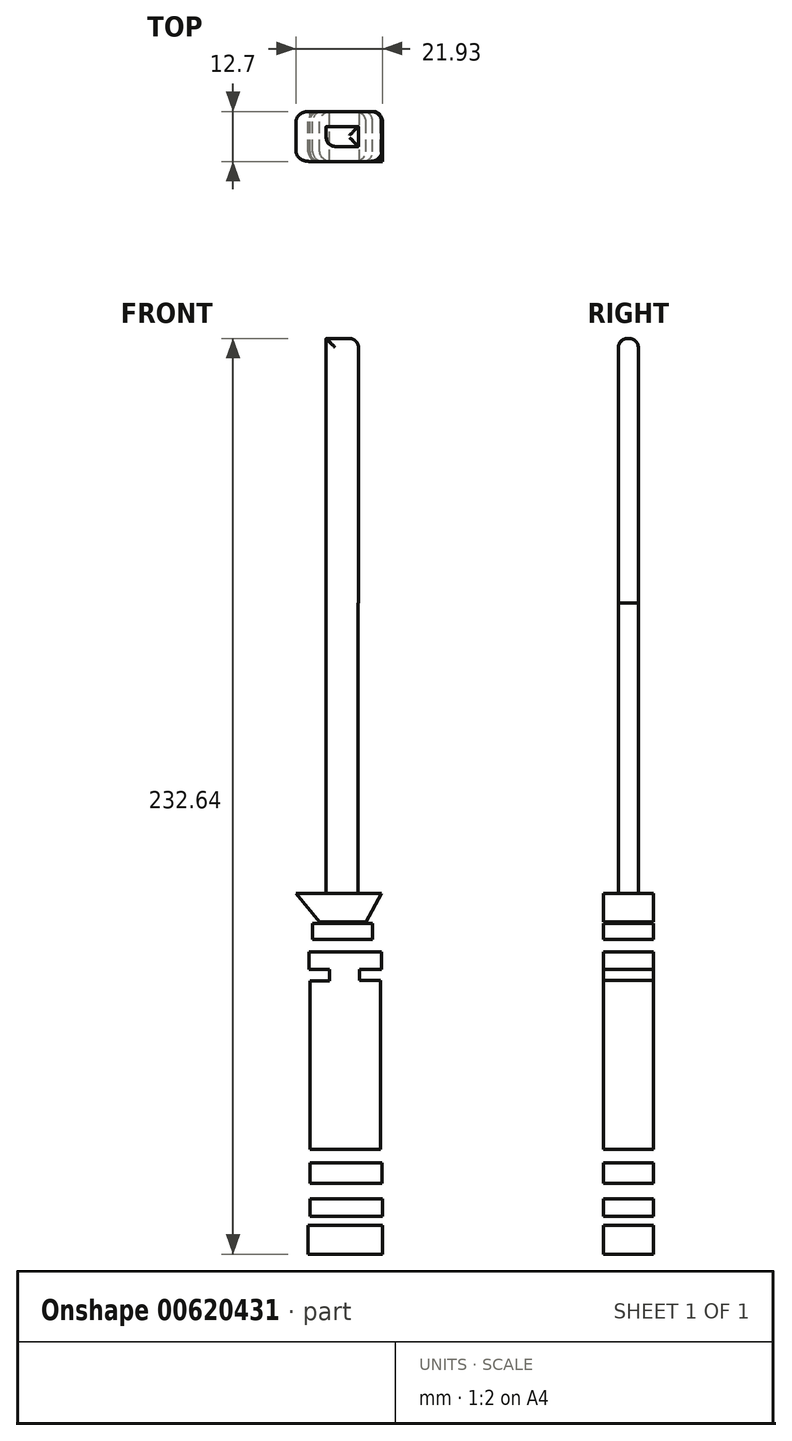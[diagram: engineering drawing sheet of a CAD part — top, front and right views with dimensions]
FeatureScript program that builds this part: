
annotation { "Feature Type Name" : "Feature", "Feature Type Description" : "" }
export const myFeature = defineFeature(function(context is Context, id is Id, definition is map)
    precondition{}
    {
        {
            var Q0;
            Q0=qCreatedBy(makeId("Front.planeOp"),FACE);
            var sketch = newSketch(context, id + "F0", { "sketchPlane" : qUnion([Q0])});
            skLineSegment(sketch, "E0", {"start": v(-11.68, 17.85) * mm, "end": v(-5.77, 10.6) * mm});
            skLineSegment(sketch, "E1", {"start": v(-5.77, 10.6) * mm, "end": v(6.04, 10.6) * mm});
            skLineSegment(sketch, "E2", {"start": v(6.04, 10.6) * mm, "end": v(10.07, 17.85) * mm});
            skLineSegment(sketch, "E3", {"start": v(10.07, 17.85) * mm, "end": v(-11.68, 17.85) * mm});
            skPoint(sketch, "E4.middle", {"position": v(0.13, -3.36) * mm});
            skPoint(sketch, "E5", {"position": v(0.13, 10.6) * mm});
            skLineSegment(sketch, "E6.bottom", {"start": v(-7.47, 10.27) * mm, "end": v(7.78, 10.27) * mm});
            skLineSegment(sketch, "E6.top", {"start": v(-7.47, 6.2) * mm, "end": v(7.78, 6.2) * mm});
            skLineSegment(sketch, "E6.left", {"start": v(-7.47, 10.27) * mm, "end": v(-7.47, 6.2) * mm});
            skLineSegment(sketch, "E6.right", {"start": v(7.78, 10.27) * mm, "end": v(7.78, 6.2) * mm});
            skLineSegment(sketch, "E7.bottom", {"start": v(-3.36, 6.2) * mm, "end": v(4.43, 6.2) * mm});
            skLineSegment(sketch, "E7.top", {"start": v(-3.36, 3.09) * mm, "end": v(4.43, 3.09) * mm});
            skLineSegment(sketch, "E7.left", {"start": v(-3.36, 6.2) * mm, "end": v(-3.36, 3.09) * mm});
            skLineSegment(sketch, "E7.right", {"start": v(4.43, 6.2) * mm, "end": v(4.43, 3.09) * mm});
            skLineSegment(sketch, "E8.bottom", {"start": v(-8.46, 3.09) * mm, "end": v(9.99, 3.09) * mm});
            skLineSegment(sketch, "E8.top", {"start": v(-8.46, -1.43) * mm, "end": v(9.99, -1.43) * mm});
            skLineSegment(sketch, "E8.left", {"start": v(-8.46, 3.09) * mm, "end": v(-8.46, -1.43) * mm});
            skLineSegment(sketch, "E8.right", {"start": v(9.99, 3.09) * mm, "end": v(9.99, -1.43) * mm});
            skLineSegment(sketch, "E9", {"start": v(-3.22, -1.43) * mm, "end": v(-3.22, -4.32) * mm});
            skLineSegment(sketch, "E10", {"start": v(-3.22, -4.32) * mm, "end": v(-8.17, -4.32) * mm});
            skLineSegment(sketch, "E11", {"start": v(-8.17, -4.32) * mm, "end": v(-8.17, -47.12) * mm});
            skLineSegment(sketch, "E12", {"start": v(-8.17, -47.12) * mm, "end": v(9.8, -47.12) * mm});
            skLineSegment(sketch, "E13", {"start": v(9.8, -47.12) * mm, "end": v(9.8, -4.16) * mm});
            skLineSegment(sketch, "E14", {"start": v(9.8, -4.16) * mm, "end": v(4.43, -4.16) * mm});
            skLineSegment(sketch, "E15", {"start": v(4.43, -4.16) * mm, "end": v(4.43, 0) * mm});
            skLineSegment(sketch, "E16.bottom", {"start": v(-3.6, -47.12) * mm, "end": v(5.72, -47.12) * mm});
            skLineSegment(sketch, "E16.top", {"start": v(-3.6, -50.57) * mm, "end": v(5.72, -50.57) * mm});
            skLineSegment(sketch, "E16.left", {"start": v(-3.6, -47.12) * mm, "end": v(-3.6, -50.57) * mm});
            skLineSegment(sketch, "E16.right", {"start": v(5.72, -47.12) * mm, "end": v(5.72, -50.57) * mm});
            skLineSegment(sketch, "E17.bottom", {"start": v(-8.17, -50.57) * mm, "end": v(10.16, -50.57) * mm});
            skLineSegment(sketch, "E17.top", {"start": v(-8.17, -55.74) * mm, "end": v(10.16, -55.74) * mm});
            skLineSegment(sketch, "E17.left", {"start": v(-8.17, -50.57) * mm, "end": v(-8.17, -55.74) * mm});
            skLineSegment(sketch, "E17.right", {"start": v(10.16, -50.57) * mm, "end": v(10.16, -55.74) * mm});
            skLineSegment(sketch, "E18.bottom", {"start": v(-3.37, -55.74) * mm, "end": v(5.72, -55.74) * mm});
            skLineSegment(sketch, "E18.top", {"start": v(-3.37, -59.71) * mm, "end": v(5.72, -59.71) * mm});
            skLineSegment(sketch, "E18.left", {"start": v(-3.37, -55.74) * mm, "end": v(-3.37, -59.71) * mm});
            skLineSegment(sketch, "E18.right", {"start": v(5.72, -55.74) * mm, "end": v(5.72, -59.71) * mm});
            skLineSegment(sketch, "E19.bottom", {"start": v(-8.2, -59.75) * mm, "end": v(10.25, -59.75) * mm});
            skLineSegment(sketch, "E19.top", {"start": v(-8.2, -64.2) * mm, "end": v(10.25, -64.2) * mm});
            skLineSegment(sketch, "E19.left", {"start": v(-8.2, -59.75) * mm, "end": v(-8.2, -64.2) * mm});
            skLineSegment(sketch, "E19.right", {"start": v(10.25, -59.75) * mm, "end": v(10.25, -64.2) * mm});
            skLineSegment(sketch, "E20.bottom", {"start": v(-5.75, -64.2) * mm, "end": v(7.8, -64.2) * mm});
            skLineSegment(sketch, "E20.top", {"start": v(-5.75, -66.42) * mm, "end": v(7.8, -66.42) * mm});
            skLineSegment(sketch, "E20.left", {"start": v(-5.75, -64.2) * mm, "end": v(-5.75, -66.42) * mm});
            skLineSegment(sketch, "E20.right", {"start": v(7.8, -64.2) * mm, "end": v(7.8, -66.42) * mm});
            skLineSegment(sketch, "E21.bottom", {"start": v(-8.64, -66.42) * mm, "end": v(10.25, -66.42) * mm});
            skLineSegment(sketch, "E21.top", {"start": v(-8.64, -73.75) * mm, "end": v(10.25, -73.75) * mm});
            skLineSegment(sketch, "E21.left", {"start": v(-8.64, -66.42) * mm, "end": v(-8.64, -73.75) * mm});
            skLineSegment(sketch, "E21.right", {"start": v(10.25, -66.42) * mm, "end": v(10.25, -73.75) * mm});
            skSolve(sketch);
        }
        {
            var Q0;
            Q0=makeQuery(id+"F0.imprint","IMPRINT",FACE,{"disambiguationData":[TD([[makeQuery(id+"F0.imprint","IMPRINT",EDGE,{"derivedFrom":sQuery(id+"F0.wireOp",EDGE,"E0")}),1.0]])]});
            var Q1;
            Q1=makeQuery(id+"F0.imprint","IMPRINT",FACE,{"disambiguationData":[TD([[makeQuery(id+"F0.imprint","IMPRINT",EDGE,{"derivedFrom":sQuery(id+"F0.wireOp",EDGE,"E6.bottom")}),-1.0]])]});
            var Q2;
            Q2=makeQuery(id+"F0.imprint","IMPRINT",FACE,{"disambiguationData":[TD([[makeQuery(id+"F0.imprint","IMPRINT",EDGE,{"derivedFrom":sQuery(id+"F0.wireOp",EDGE,"E7.bottom")}),-1.0]])]});
            var Q3;
            {var subQ0=sQuery(id+"F0.wireOp",EDGE,"E8.left");Q3=makeQuery(id+"F0.imprint","IMPRINT",FACE,{"disambiguationData":[TD([[makeQuery(id+"F0.imprint","IMPRINT",EDGE,{"derivedFrom":subQ0}),1.0]])]});}
            var Q4;
            {var subQ1=sQuery(id+"F0.wireOp",EDGE,"E9");Q4=makeQuery(id+"F0.imprint","IMPRINT",FACE,{"disambiguationData":[TD([[makeQuery(id+"F0.imprint","IMPRINT",EDGE,{"derivedFrom":subQ1}),1.0]])]});}
            var Q5;
            Q5=makeQuery(id+"F0.imprint","IMPRINT",FACE,{"disambiguationData":[TD([[makeQuery(id+"F0.imprint","IMPRINT",EDGE,{"derivedFrom":sQuery(id+"F0.wireOp",EDGE,"E16.bottom")}),-1.0]])]});
            var Q6;
            {var subQ0=sQuery(id+"F0.wireOp",EDGE,"E17.left");Q6=makeQuery(id+"F0.imprint","IMPRINT",FACE,{"disambiguationData":[TD([[makeQuery(id+"F0.imprint","IMPRINT",EDGE,{"derivedFrom":subQ0}),1.0]])]});}
            var Q7;
            Q7=makeQuery(id+"F0.imprint","IMPRINT",FACE,{"disambiguationData":[TD([[makeQuery(id+"F0.imprint","IMPRINT",EDGE,{"derivedFrom":sQuery(id+"F0.wireOp",EDGE,"E18.bottom")}),-1.0]])]});
            var Q8;
            Q8=makeQuery(id+"F0.imprint","IMPRINT",FACE,{"disambiguationData":[TD([[makeQuery(id+"F0.imprint","IMPRINT",EDGE,{"derivedFrom":sQuery(id+"F0.wireOp",EDGE,"E19.bottom")}),-1.0]])]});
            var Q9;
            Q9=makeQuery(id+"F0.imprint","IMPRINT",FACE,{"disambiguationData":[TD([[makeQuery(id+"F0.imprint","IMPRINT",EDGE,{"derivedFrom":sQuery(id+"F0.wireOp",EDGE,"E20.bottom")}),-1.0]])]});
            var Q10;
            Q10=makeQuery(id+"F0.imprint","IMPRINT",FACE,{"disambiguationData":[TD([[makeQuery(id+"F0.imprint","IMPRINT",EDGE,{"derivedFrom":sQuery(id+"F0.wireOp",EDGE,"E21.top")}),1.0]])]});
            extrude(context, id + "F1", {"entities" : qUnion([Q0, Q1, Q2, Q3, Q4, Q5, Q6, Q7, Q8, Q9, Q10]), "endBound" : BoundingType.SYMMETRIC, "depth" : 12.7 * mm, "offsetDistance" : 25.4 * mm});
        }
        {
            var Q0;
            Q0=qCreatedBy(makeId("Front.planeOp"),FACE);
            var sketch = newSketch(context, id + "F2", { "sketchPlane" : qUnion([Q0])});
            skLineSegment(sketch, "E22.bottom", {"start": v(0, 15.52) * mm, "end": v(4.04, 15.52) * mm});
            skLineSegment(sketch, "E22.top", {"start": v(0, 91.72) * mm, "end": v(4.04, 91.72) * mm});
            skLineSegment(sketch, "E22.left", {"start": v(0, 15.52) * mm, "end": v(0, 91.72) * mm});
            skLineSegment(sketch, "E22.right", {"start": v(4.04, 15.52) * mm, "end": v(4.04, 91.72) * mm});
            skLineSegment(sketch, "E23.MirrorCS", {"start": v(-4.04, 15.52) * mm, "end": v(-4.04, 91.72) * mm});
            skLineSegment(sketch, "E24.MirrorCS", {"start": v(0, 15.52) * mm, "end": v(-4.04, 15.52) * mm});
            skLineSegment(sketch, "E25.MirrorCS", {"start": v(0, 91.72) * mm, "end": v(-4.04, 91.72) * mm});
            skLineSegment(sketch, "E26.bottom", {"start": v(-4.04, 91.72) * mm, "end": v(4.16, 91.72) * mm});
            skLineSegment(sketch, "E26.top", {"start": v(-4.04, 158.9) * mm, "end": v(4.16, 158.9) * mm});
            skLineSegment(sketch, "E26.left", {"start": v(-4.04, 91.72) * mm, "end": v(-4.04, 158.9) * mm});
            skLineSegment(sketch, "E26.right", {"start": v(4.16, 91.72) * mm, "end": v(4.16, 158.9) * mm});
            skSolve(sketch);
        }
        {
            var Q0;
            Q0=makeQuery(id+"F1.opExtrude","CAP_EDGE",EDGE,{"disambiguationData":[OSD([sQuery(id+"F0.wireOp",EDGE,"E8.right")])],"isStart":false});
            var Q1;
            Q1=makeQuery(id+"F1.opExtrude","CAP_EDGE",EDGE,{"disambiguationData":[OSD([sQuery(id+"F0.wireOp",EDGE,"E8.left")])],"isStart":false});
            var Q2;
            Q2=makeQuery(id+"F1.opExtrude","CAP_EDGE",EDGE,{"disambiguationData":[OSD([sQuery(id+"F0.wireOp",EDGE,"E6.left")])],"isStart":false});
            var Q3;
            Q3=makeQuery(id+"F1.opExtrude","CAP_EDGE",EDGE,{"disambiguationData":[OSD([sQuery(id+"F0.wireOp",EDGE,"E6.right")])],"isStart":false});
            var Q4;
            Q4=makeQuery(id+"F1.opExtrude","CAP_EDGE",EDGE,{"disambiguationData":[OSD([sQuery(id+"F0.wireOp",EDGE,"E6.right")])],"isStart":true});
            var Q5;
            Q5=makeQuery(id+"F1.opExtrude","CAP_EDGE",EDGE,{"disambiguationData":[OSD([sQuery(id+"F0.wireOp",EDGE,"E8.right")])],"isStart":true});
            var Q6;
            Q6=makeQuery(id+"F1.opExtrude","CAP_EDGE",EDGE,{"disambiguationData":[OSD([sQuery(id+"F0.wireOp",EDGE,"E8.left")])],"isStart":true});
            var Q7;
            Q7=makeQuery(id+"F1.opExtrude","CAP_EDGE",EDGE,{"disambiguationData":[OSD([sQuery(id+"F0.wireOp",EDGE,"E6.left")])],"isStart":true});
            var Q8;
            Q8=makeQuery(id+"F1.opExtrude","CAP_EDGE",EDGE,{"disambiguationData":[OSD([sQuery(id+"F0.wireOp",EDGE,"E17.right")])],"isStart":false});
            var Q9;
            Q9=makeQuery(id+"F1.opExtrude","CAP_EDGE",EDGE,{"disambiguationData":[OSD([sQuery(id+"F0.wireOp",EDGE,"E17.right")])],"isStart":true});
            var Q10;
            Q10=makeQuery(id+"F1.opExtrude","CAP_EDGE",EDGE,{"disambiguationData":[OSD([sQuery(id+"F0.wireOp",EDGE,"E19.right")])],"isStart":false});
            var Q11;
            Q11=makeQuery(id+"F1.opExtrude","CAP_EDGE",EDGE,{"disambiguationData":[OSD([sQuery(id+"F0.wireOp",EDGE,"E17.left")])],"isStart":false});
            var Q12;
            Q12=makeQuery(id+"F1.opExtrude","CAP_EDGE",EDGE,{"disambiguationData":[OSD([sQuery(id+"F0.wireOp",EDGE,"E19.left")])],"isStart":false});
            var Q13;
            Q13=makeQuery(id+"F1.opExtrude","CAP_EDGE",EDGE,{"disambiguationData":[OSD([sQuery(id+"F0.wireOp",EDGE,"E21.left")])],"isStart":false});
            var Q14;
            Q14=makeQuery(id+"F1.opExtrude","CAP_EDGE",EDGE,{"disambiguationData":[OSD([sQuery(id+"F0.wireOp",EDGE,"E19.right")])],"isStart":true});
            var Q15;
            Q15=makeQuery(id+"F1.opExtrude","CAP_EDGE",EDGE,{"disambiguationData":[OSD([sQuery(id+"F0.wireOp",EDGE,"E21.right")])],"isStart":true});
            var Q16;
            Q16=makeQuery(id+"F1.opExtrude","CAP_EDGE",EDGE,{"disambiguationData":[OSD([sQuery(id+"F0.wireOp",EDGE,"E21.left")])],"isStart":true});
            var Q17;
            Q17=makeQuery(id+"F1.opExtrude","CAP_EDGE",EDGE,{"disambiguationData":[OSD([sQuery(id+"F0.wireOp",EDGE,"E19.left")])],"isStart":true});
            var Q18;
            Q18=makeQuery(id+"F1.opExtrude","CAP_EDGE",EDGE,{"disambiguationData":[OSD([sQuery(id+"F0.wireOp",EDGE,"E17.left")])],"isStart":true});
            var Q19;
            Q19=makeQuery(id+"F1.opExtrude","CAP_EDGE",EDGE,{"disambiguationData":[OSD([sQuery(id+"F0.wireOp",EDGE,"E11")])],"isStart":false});
            var Q20;
            Q20=makeQuery(id+"F1.opExtrude","CAP_EDGE",EDGE,{"disambiguationData":[OSD([sQuery(id+"F0.wireOp",EDGE,"E13")])],"isStart":false});
            var Q21;
            Q21=makeQuery(id+"F1.opExtrude","CAP_EDGE",EDGE,{"disambiguationData":[OSD([sQuery(id+"F0.wireOp",EDGE,"E13")])],"isStart":true});
            var Q22;
            Q22=makeQuery(id+"F1.opExtrude","CAP_EDGE",EDGE,{"disambiguationData":[OSD([sQuery(id+"F0.wireOp",EDGE,"E0")])],"isStart":false});
            var Q23;
            Q23=makeQuery(id+"F1.opExtrude","CAP_EDGE",EDGE,{"disambiguationData":[OSD([sQuery(id+"F0.wireOp",EDGE,"E2")])],"isStart":false});
            var Q24;
            Q24=makeQuery(id+"F1.opExtrude","CAP_EDGE",EDGE,{"disambiguationData":[OSD([sQuery(id+"F0.wireOp",EDGE,"E2")])],"isStart":true});
            var Q25;
            Q25=makeQuery(id+"F1.opExtrude","CAP_EDGE",EDGE,{"disambiguationData":[OSD([sQuery(id+"F0.wireOp",EDGE,"E0")])],"isStart":true});
            fillet(context, id + "F3", {"entities" : qUnion([Q0, Q1, Q2, Q3, Q4, Q5, Q6, Q7, Q8, Q9, Q10, Q11, Q12, Q13, Q14, Q15, Q16, Q17, Q18, Q19, Q20, Q21, Q22, Q23, Q24, Q25]), "radius" : 2.54 * mm, "tangentPropagation" : true, "allowEdgeOverflow" : false});
        }
        {
            var Q0;
            Q0=makeQuery(id+"F2.imprint","IMPRINT",FACE,{"disambiguationData":[TD([[makeQuery(id+"F2.imprint","IMPRINT",EDGE,{"derivedFrom":sQuery(id+"F2.wireOp",EDGE,"E22.bottom")}),1.0]])]});
            var Q1;
            Q1=makeQuery(id+"F2.imprint","IMPRINT",FACE,{"disambiguationData":[TD([[makeQuery(id+"F2.imprint","IMPRINT",EDGE,{"derivedFrom":sQuery(id+"F2.wireOp",EDGE,"E22.left")}),1.0]])]});
            var Q2;
            Q2=makeQuery(id+"F2.imprint","IMPRINT",FACE,{"disambiguationData":[TD([[makeQuery(id+"F2.imprint","IMPRINT",EDGE,{"derivedFrom":sQuery(id+"F2.wireOp",EDGE,"E26.top")}),-1.0]])]});
            extrude(context, id + "F4", {"entities" : qUnion([Q0, Q1, Q2]), "operationType" : NewBodyOperationType.ADD, "endBound" : BoundingType.SYMMETRIC, "depth" : 5.08 * mm, "offsetDistance" : 25.4 * mm});
        }
        {
            var Q0;
            Q0=makeQuery(id+"F4.opExtrude","SWEPT_EDGE",EDGE,{"disambiguationData":[OSD([sQuery(id+"F2.wireOp",EDGE,"E26.top"),sQuery(id+"F2.wireOp",EDGE,"E26.left")])]});
            var Q1;
            Q1=makeQuery(id+"F4.opExtrude","CAP_EDGE",EDGE,{"disambiguationData":[OSD([sQuery(id+"F2.wireOp",EDGE,"E22.right")])],"isStart":false});
            var Q2;
            Q2=makeQuery(id+"F4.opExtrude","CAP_EDGE",EDGE,{"disambiguationData":[OSD([sQuery(id+"F2.wireOp",EDGE,"E26.right")])],"isStart":false});
            var Q3;
            Q3=makeQuery(id+"F4.opExtrude","CAP_EDGE",EDGE,{"disambiguationData":[OSD([sQuery(id+"F2.wireOp",EDGE,"E26.right")])],"isStart":true});
            var Q4;
            Q4=makeQuery(id+"F4.opExtrude","CAP_EDGE",EDGE,{"disambiguationData":[OSD([sQuery(id+"F2.wireOp",EDGE,"E22.right")])],"isStart":true});
            var Q5;
            Q5=makeQuery(id+"F4.opExtrude","CAP_EDGE",EDGE,{"disambiguationData":[OSD([sQuery(id+"F2.wireOp",EDGE,"E23.MirrorCS"),sQuery(id+"F2.wireOp",EDGE,"E26.left")])],"isStart":true});
            fillet(context, id + "F5", {"entities" : qUnion([Q0, Q1, Q2, Q3, Q4, Q5]), "radius" : 0.03 * mm, "tangentPropagation" : true, "allowEdgeOverflow" : false});
        }
        {
            var Q0;
            Q0=makeQuery(id+"F4.opExtrude","CAP_EDGE",EDGE,{"disambiguationData":[OSD([sQuery(id+"F2.wireOp",EDGE,"E26.top")])],"isStart":true});
            var Q1;
            Q1=makeQuery(id+"F4.opExtrude","CAP_EDGE",EDGE,{"disambiguationData":[OSD([sQuery(id+"F2.wireOp",EDGE,"E26.top")])],"isStart":false});
            var Q2;
            {var subQ0=sQuery(id+"F2.wireOp",EDGE,"E22.right");Q2=makeQuery(id+"F5.opFillet","BLEND_EDGE",EDGE,{"blendedFrom":[makeQuery(id+"F4.opExtrude","CAP_EDGE",EDGE,{"disambiguationData":[OSD([subQ0])],"isStart":false}),makeQuery(id+"F4.opExtrude","CAP_FACE",FACE,{"disambiguationData":[OSD([sQuery(id+"F2.wireOp",EDGE,"E22.bottom"),subQ0,sQuery(id+"F2.wireOp",EDGE,"E23.MirrorCS"),sQuery(id+"F2.wireOp",EDGE,"E24.MirrorCS"),sQuery(id+"F2.wireOp",EDGE,"E26.bottom"),sQuery(id+"F2.wireOp",EDGE,"E26.top"),sQuery(id+"F2.wireOp",EDGE,"E26.left"),sQuery(id+"F2.wireOp",EDGE,"E26.right")])],"isStart":false})],"blendedInto":[makeQuery(id+"F4.opExtrude","CAP_FACE",FACE,{"disambiguationData":[OSD([sQuery(id+"F2.wireOp",EDGE,"E22.bottom"),subQ0,sQuery(id+"F2.wireOp",EDGE,"E23.MirrorCS"),sQuery(id+"F2.wireOp",EDGE,"E24.MirrorCS"),sQuery(id+"F2.wireOp",EDGE,"E26.bottom"),sQuery(id+"F2.wireOp",EDGE,"E26.top"),sQuery(id+"F2.wireOp",EDGE,"E26.left"),sQuery(id+"F2.wireOp",EDGE,"E26.right")])],"isStart":false})]});}
            var Q3;
            {var subQ0=sQuery(id+"F2.wireOp",EDGE,"E26.right");Q3=makeQuery(id+"F5.opFillet","BLEND_EDGE",EDGE,{"blendedFrom":[makeQuery(id+"F4.opExtrude","CAP_EDGE",EDGE,{"disambiguationData":[OSD([subQ0])],"isStart":false}),makeQuery(id+"F4.opExtrude","CAP_FACE",FACE,{"disambiguationData":[OSD([sQuery(id+"F2.wireOp",EDGE,"E22.bottom"),sQuery(id+"F2.wireOp",EDGE,"E22.right"),sQuery(id+"F2.wireOp",EDGE,"E23.MirrorCS"),sQuery(id+"F2.wireOp",EDGE,"E24.MirrorCS"),sQuery(id+"F2.wireOp",EDGE,"E26.bottom"),sQuery(id+"F2.wireOp",EDGE,"E26.top"),sQuery(id+"F2.wireOp",EDGE,"E26.left"),subQ0])],"isStart":false})],"blendedInto":[makeQuery(id+"F4.opExtrude","CAP_FACE",FACE,{"disambiguationData":[OSD([sQuery(id+"F2.wireOp",EDGE,"E22.bottom"),sQuery(id+"F2.wireOp",EDGE,"E22.right"),sQuery(id+"F2.wireOp",EDGE,"E23.MirrorCS"),sQuery(id+"F2.wireOp",EDGE,"E24.MirrorCS"),sQuery(id+"F2.wireOp",EDGE,"E26.bottom"),sQuery(id+"F2.wireOp",EDGE,"E26.top"),sQuery(id+"F2.wireOp",EDGE,"E26.left"),subQ0])],"isStart":false})]});}
            var Q4;
            {var subQ0=sQuery(id+"F2.wireOp",EDGE,"E22.right");Q4=makeQuery(id+"F5.opFillet","BLEND_EDGE",EDGE,{"blendedFrom":[makeQuery(id+"F4.opExtrude","CAP_EDGE",EDGE,{"disambiguationData":[OSD([subQ0])],"isStart":true}),makeQuery(id+"F4.opExtrude","CAP_FACE",FACE,{"disambiguationData":[OSD([sQuery(id+"F2.wireOp",EDGE,"E22.bottom"),subQ0,sQuery(id+"F2.wireOp",EDGE,"E23.MirrorCS"),sQuery(id+"F2.wireOp",EDGE,"E24.MirrorCS"),sQuery(id+"F2.wireOp",EDGE,"E26.bottom"),sQuery(id+"F2.wireOp",EDGE,"E26.top"),sQuery(id+"F2.wireOp",EDGE,"E26.left"),sQuery(id+"F2.wireOp",EDGE,"E26.right")])],"isStart":true})],"blendedInto":[makeQuery(id+"F4.opExtrude","CAP_FACE",FACE,{"disambiguationData":[OSD([sQuery(id+"F2.wireOp",EDGE,"E22.bottom"),subQ0,sQuery(id+"F2.wireOp",EDGE,"E23.MirrorCS"),sQuery(id+"F2.wireOp",EDGE,"E24.MirrorCS"),sQuery(id+"F2.wireOp",EDGE,"E26.bottom"),sQuery(id+"F2.wireOp",EDGE,"E26.top"),sQuery(id+"F2.wireOp",EDGE,"E26.left"),sQuery(id+"F2.wireOp",EDGE,"E26.right")])],"isStart":true})]});}
            var Q5;
            {var subQ0=sQuery(id+"F2.wireOp",EDGE,"E26.right");Q5=makeQuery(id+"F5.opFillet","BLEND_EDGE",EDGE,{"blendedFrom":[makeQuery(id+"F4.opExtrude","CAP_EDGE",EDGE,{"disambiguationData":[OSD([subQ0])],"isStart":true}),makeQuery(id+"F4.opExtrude","SWEPT_FACE",FACE,{"disambiguationData":[OSD([subQ0])]})],"blendedInto":[makeQuery(id+"F4.opExtrude","SWEPT_FACE",FACE,{"disambiguationData":[OSD([subQ0])]})]});}
            var Q6;
            {var subQ0=sQuery(id+"F2.wireOp",EDGE,"E26.left");var subQ1=sQuery(id+"F2.wireOp",EDGE,"E23.MirrorCS");Q6=makeQuery(id+"F5.opFillet","BLEND_EDGE",EDGE,{"blendedFrom":[makeQuery(id+"F4.opExtrude","CAP_EDGE",EDGE,{"disambiguationData":[OSD([subQ1,subQ0])],"isStart":true}),makeQuery(id+"F4.opExtrude","SWEPT_FACE",FACE,{"disambiguationData":[OSD([subQ1,subQ0])]})],"blendedInto":[makeQuery(id+"F4.opExtrude","SWEPT_FACE",FACE,{"disambiguationData":[OSD([subQ1,subQ0])]})]});}
            var Q7;
            Q7=makeQuery(id+"F4.opExtrude","CAP_EDGE",EDGE,{"disambiguationData":[OSD([sQuery(id+"F2.wireOp",EDGE,"E23.MirrorCS"),sQuery(id+"F2.wireOp",EDGE,"E26.left")])],"isStart":false});
            fillet(context, id + "F6", {"entities" : qUnion([Q0, Q1, Q2, Q3, Q4, Q5, Q6, Q7]), "radius" : 2.3 * mm, "tangentPropagation" : true, "allowEdgeOverflow" : false});
        }
    });
